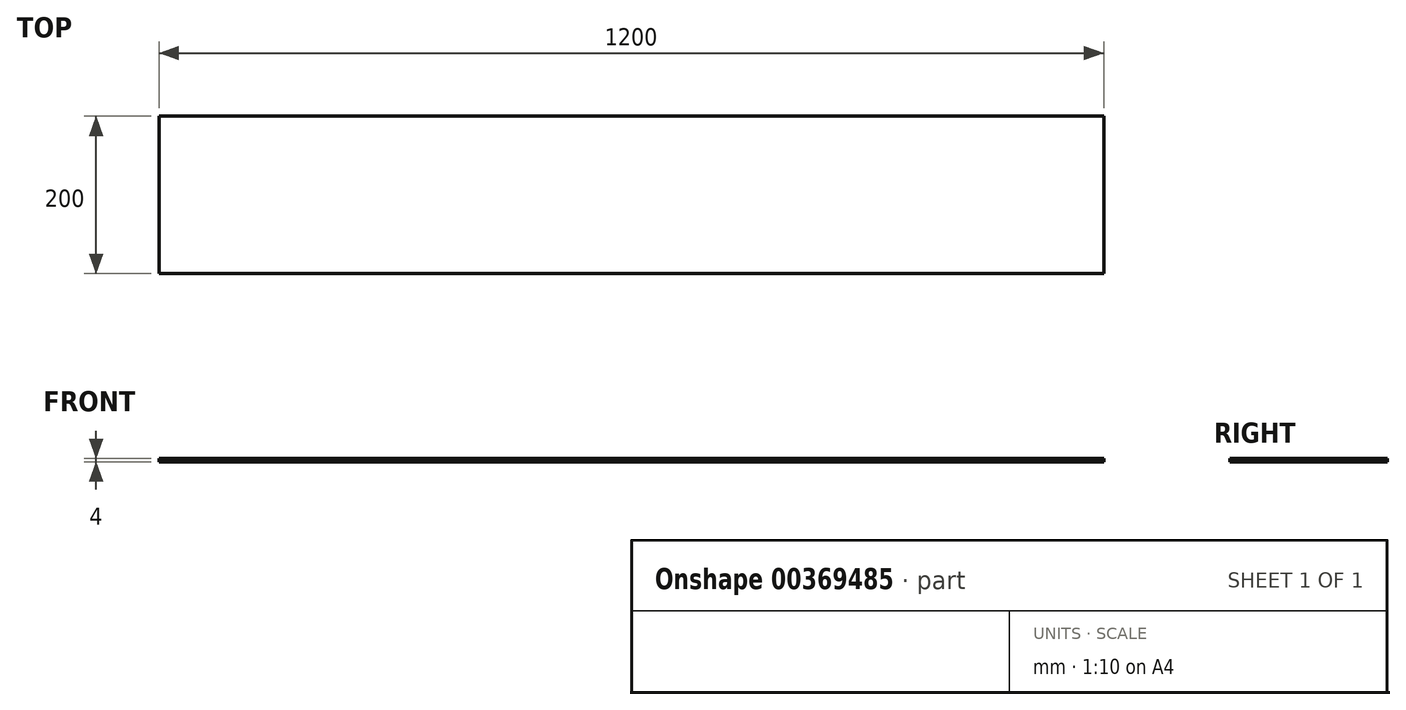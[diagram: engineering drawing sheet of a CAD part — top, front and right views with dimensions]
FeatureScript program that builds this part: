
annotation { "Feature Type Name" : "Feature", "Feature Type Description" : "" }
export const myFeature = defineFeature(function(context is Context, id is Id, definition is map)
    precondition{}
    {
        {
            var Q0;
            Q0=qCreatedBy(makeId("Top.planeOp"),FACE);
            var sketch = newSketch(context, id + "F0", { "sketchPlane" : qUnion([Q0])});
            skLineSegment(sketch, "E0.bottom", {"start": v(600, 100) * mm, "end": v(-600, 100) * mm});
            skLineSegment(sketch, "E0.top", {"start": v(600, -100) * mm, "end": v(-600, -100) * mm});
            skLineSegment(sketch, "E0.left", {"start": v(600, 100) * mm, "end": v(600, -100) * mm});
            skLineSegment(sketch, "E0.right", {"start": v(-600, 100) * mm, "end": v(-600, -100) * mm});
            skPoint(sketch, "E0.middle", {"position": v(0, 0) * mm});
            skSolve(sketch);
        }
        {
            var Q0;
            Q0 = qSketchRegion(id + "F0", true);
            extrude(context, id + "F1", {"entities" : qUnion([Q0]), "depth" : 4 * mm});
        }
    });
